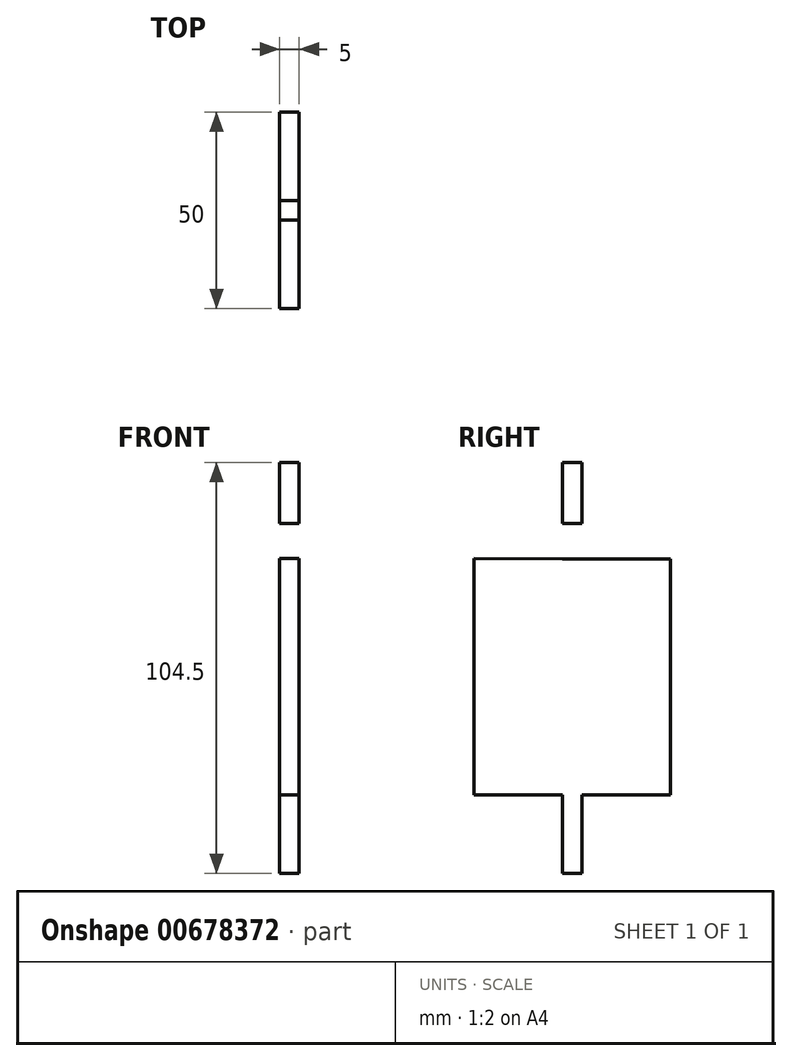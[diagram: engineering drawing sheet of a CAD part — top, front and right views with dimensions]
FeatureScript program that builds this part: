
annotation { "Feature Type Name" : "Feature", "Feature Type Description" : "" }
export const myFeature = defineFeature(function(context is Context, id is Id, definition is map)
    precondition{}
    {
        {
            var Q0;
            Q0=qCreatedBy(makeId("Right.planeOp"),FACE);
            var sketch = newSketch(context, id + "F0", { "sketchPlane" : qUnion([Q0])});
            skLineSegment(sketch, "E0", {"start": v(0, 0) * mm, "end": v(0, -60) * mm});
            skLineSegment(sketch, "E1", {"start": v(0, -60) * mm, "end": v(12.4, -60) * mm});
            skLineSegment(sketch, "E2.0", {"start": v(27.5, -60) * mm, "end": v(27.5, -81.07) * mm});
            skLineSegment(sketch, "E3", {"start": v(12, -60) * mm, "end": v(12.4, -60) * mm});
            skLineSegment(sketch, "E4", {"start": v(0, -60) * mm, "end": v(12, -60) * mm});
            skLineSegment(sketch, "E5", {"start": v(22.5, -80) * mm, "end": v(22.5, -60) * mm});
            skPoint(sketch, "E6.trimOffspring.start.orphan", {"position": v(25, -60) * mm});
            skLineSegment(sketch, "E7", {"start": v(27.5, -80) * mm, "end": v(27.5, -81.07) * mm});
            skLineSegment(sketch, "E8", {"start": v(22.5, -80) * mm, "end": v(27.5, -80) * mm});
            skLineSegment(sketch, "E9", {"start": v(11.37, -27.14) * mm, "end": v(11.37, -26.74) * mm});
            skLineSegment(sketch, "E10", {"start": v(38.63, -27.14) * mm, "end": v(38.63, -26.74) * mm});
            skLineSegment(sketch, "E11", {"start": v(0, -60) * mm, "end": v(22.5, -60) * mm});
            skLineSegment(sketch, "E12.trimOffspring", {"start": v(22.5, -60) * mm, "end": v(0, -60) * mm});
            skLineSegment(sketch, "E13", {"start": v(22.5, -0.04) * mm, "end": v(0, 0) * mm});
            skLineSegment(sketch, "E14.0", {"start": v(50, -0.04) * mm, "end": v(50, -60) * mm});
            skLineSegment(sketch, "E15", {"start": v(50, -0.04) * mm, "end": v(22.5, -0.04) * mm});
            skLineSegment(sketch, "E16", {"start": v(50, -60) * mm, "end": v(27.5, -60) * mm});
            skLineSegment(sketch, "E17", {"start": v(22.5, 9) * mm, "end": v(22.5, 24.5) * mm});
            skLineSegment(sketch, "E18", {"start": v(27.5, 24.5) * mm, "end": v(27.5, 9) * mm});
            skLineSegment(sketch, "E19.0", {"start": v(27.5, 9) * mm, "end": v(22.5, 9) * mm});
            skPoint(sketch, "E20.orphan", {"position": v(27.5, 0) * mm});
            skLineSegment(sketch, "E21", {"start": v(22.5, 24.5) * mm, "end": v(27.5, 24.5) * mm});
            skPoint(sketch, "E21.startSnap0", {"position": v(27.5, 24.5) * mm});
            skPoint(sketch, "E21.endSnap0", {"position": v(27.5, 24.5) * mm});
            skPoint(sketch, "E22.end.orphan", {"position": v(27.5, 40) * mm});
            skSolve(sketch);
        }
        {
            var Q0;
            {var subQ1=sQuery(id+"F0.wireOp",EDGE,"E0");Q0=makeQuery(id+"F0.imprint","IMPRINT",FACE,{"disambiguationData":[TD([[makeQuery(id+"F0.imprint","IMPRINT",EDGE,{"derivedFrom":subQ1}),1.0]])]});}
            var Q1;
            Q1=makeQuery(id+"F0.imprint","IMPRINT",FACE,{"disambiguationData":[TD([[makeQuery(id+"F0.imprint","IMPRINT",EDGE,{"derivedFrom":sQuery(id+"F0.wireOp",EDGE,"E17")}),-1.0]])]});
            extrude(context, id + "F1", {"entities" : qUnion([Q0, Q1]), "depth" : 5 * mm, "offsetDistance" : 25 * mm});
        }
    });
